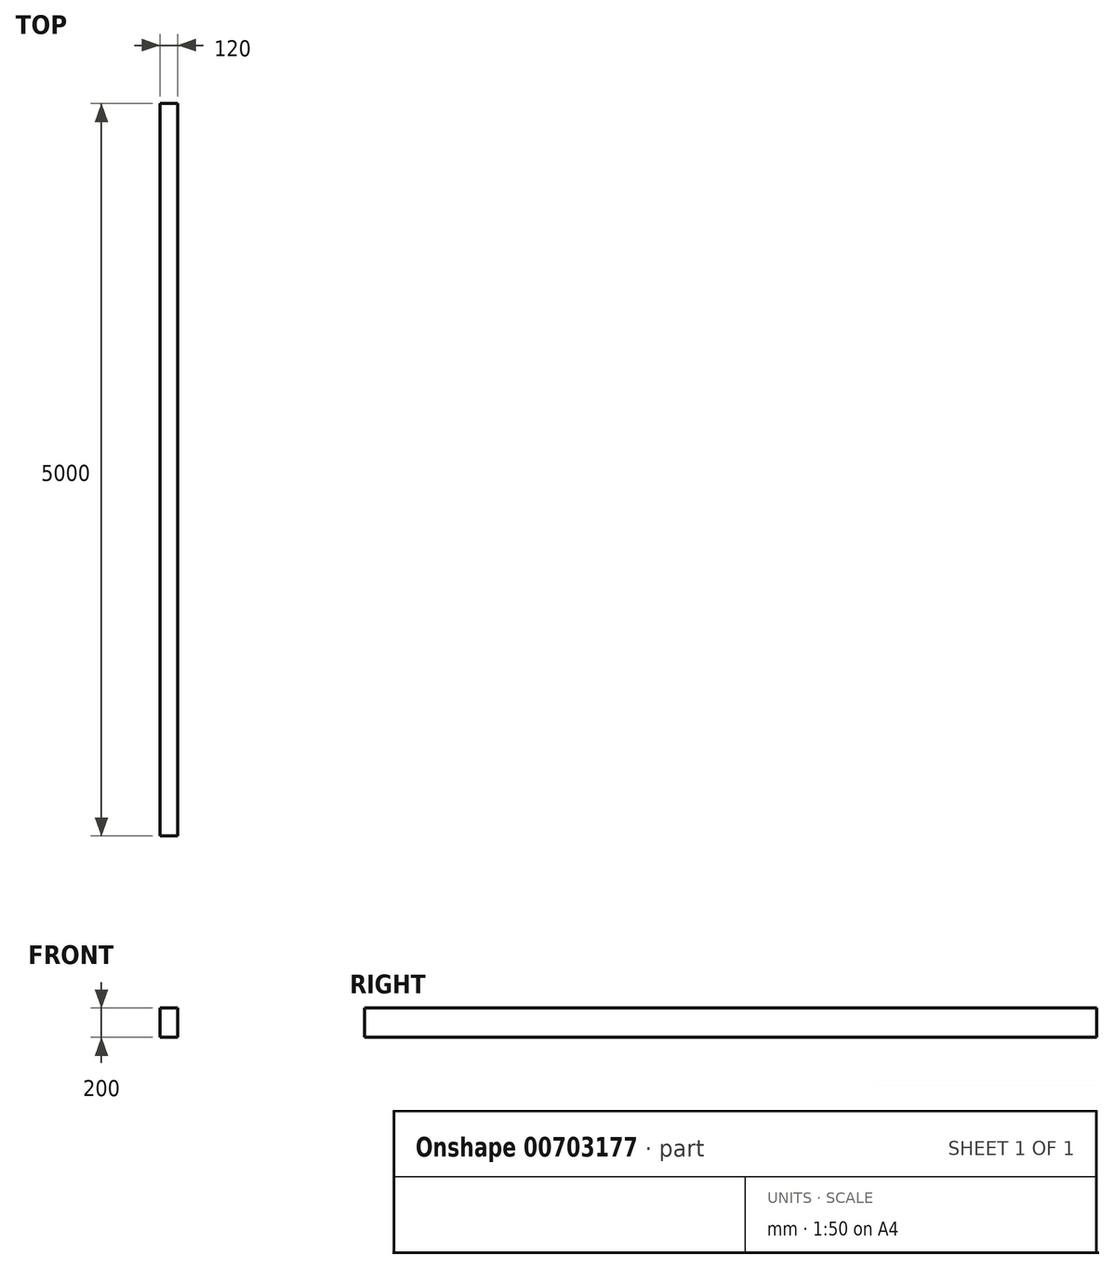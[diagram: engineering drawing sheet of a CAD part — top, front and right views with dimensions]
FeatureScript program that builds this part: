
annotation { "Feature Type Name" : "Feature", "Feature Type Description" : "" }
export const myFeature = defineFeature(function(context is Context, id is Id, definition is map)
    precondition{}
    {
        {
            var Q0;
            Q0=qCreatedBy(makeId("Front.planeOp"),FACE);
            var sketch = newSketch(context, id + "F0", { "sketchPlane" : qUnion([Q0])});
            skLineSegment(sketch, "E0.bottom", {"start": v(-68.99, 137.3) * mm, "end": v(51.01, 137.3) * mm});
            skLineSegment(sketch, "E0.top", {"start": v(-68.99, -62.7) * mm, "end": v(51.01, -62.7) * mm});
            skLineSegment(sketch, "E0.left", {"start": v(-68.99, 137.3) * mm, "end": v(-68.99, -62.7) * mm});
            skLineSegment(sketch, "E0.right", {"start": v(51.01, 137.3) * mm, "end": v(51.01, -62.7) * mm});
            skSolve(sketch);
        }
        {
            var Q0;
            Q0=makeQuery(id+"F0.imprint","IMPRINT",FACE,{"disambiguationData":[TD([[makeQuery(id+"F0.imprint","IMPRINT",EDGE,{"derivedFrom":sQuery(id+"F0.wireOp",EDGE,"E0.bottom")}),-1.0]])]});
            extrude(context, id + "F1", {"entities" : qUnion([Q0]), "depth" : 5000 * mm, "offsetDistance" : 25 * mm});
        }
    });
